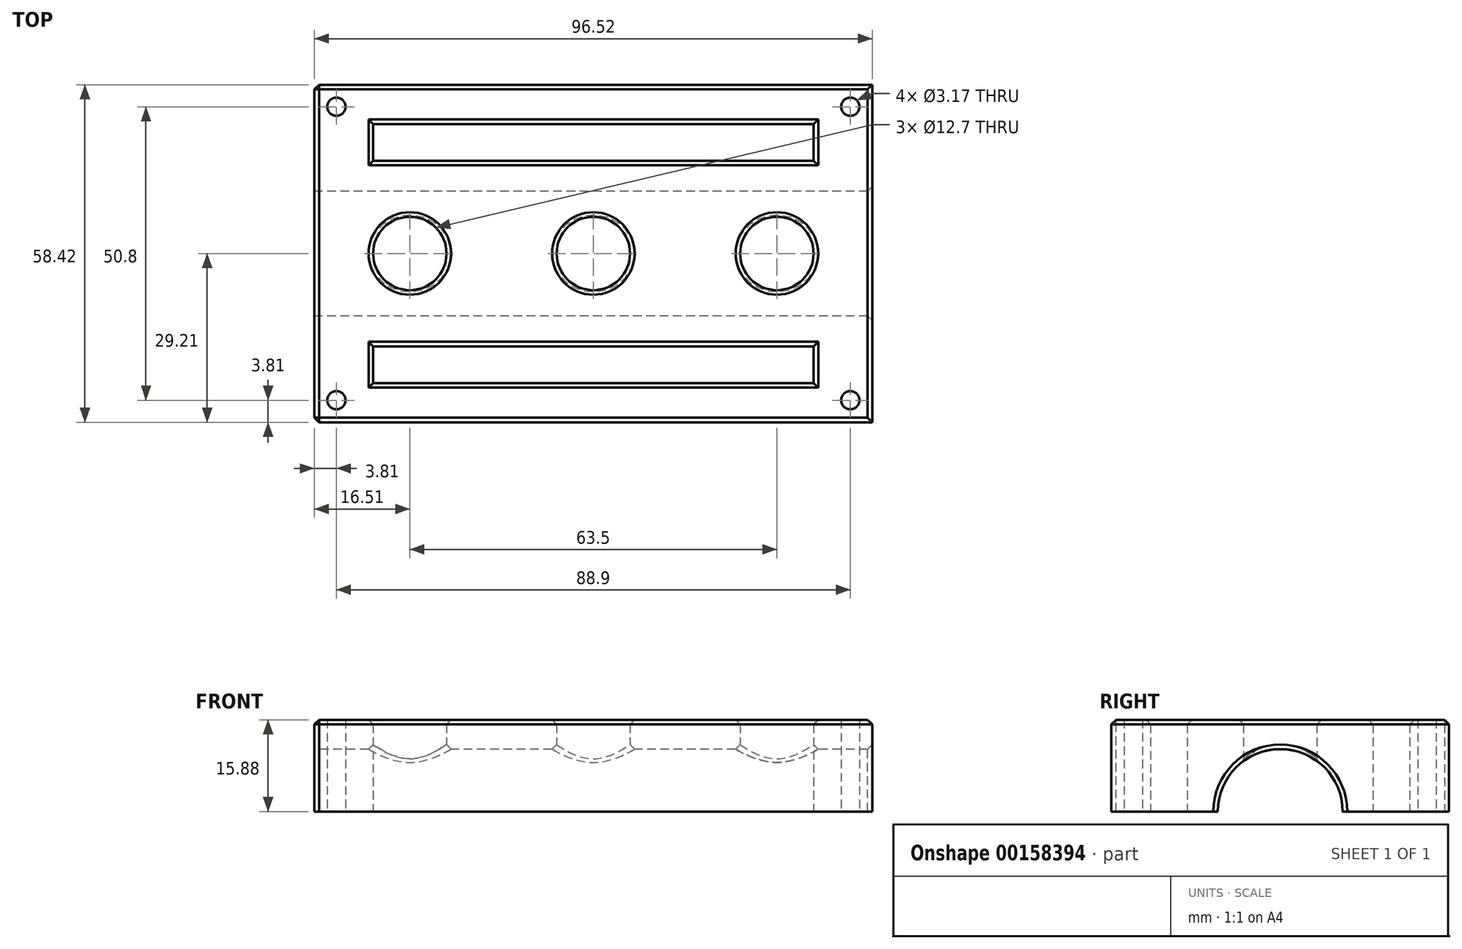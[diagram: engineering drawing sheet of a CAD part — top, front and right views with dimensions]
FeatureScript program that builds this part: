
annotation { "Feature Type Name" : "Feature", "Feature Type Description" : "" }
export const myFeature = defineFeature(function(context is Context, id is Id, definition is map)
    precondition{}
    {
        {
            var Q0;
            Q0=qCreatedBy(makeId("Top.planeOp"),FACE);
            var sketch = newSketch(context, id + "F0", { "sketchPlane" : qUnion([Q0])});
            skLineSegment(sketch, "E0", {"start": v(0, 0) * mm, "end": v(-48.26, 0) * mm});
            skLineSegment(sketch, "E1", {"start": v(-48.26, 0) * mm, "end": v(-48.26, 29.21) * mm});
            skLineSegment(sketch, "E2", {"start": v(-48.26, 29.21) * mm, "end": v(0, 29.21) * mm});
            skLineSegment(sketch, "E3", {"start": v(0, 29.21) * mm, "end": v(0, 0) * mm});
            skLineSegment(sketch, "E4.MirrorCS", {"start": v(48.26, 29.21) * mm, "end": v(0, 29.21) * mm});
            skLineSegment(sketch, "E5.MirrorCS", {"start": v(48.26, 0) * mm, "end": v(48.26, 29.21) * mm});
            skLineSegment(sketch, "E6.MirrorCS", {"start": v(0, 0) * mm, "end": v(48.26, 0) * mm});
            skLineSegment(sketch, "E7.MirrorCS", {"start": v(-48.26, -29.21) * mm, "end": v(0, -29.21) * mm});
            skLineSegment(sketch, "E8.MirrorCS", {"start": v(48.26, -29.2) * mm, "end": v(0, -29.21) * mm});
            skLineSegment(sketch, "E9.MirrorCS", {"start": v(48.26, 0) * mm, "end": v(48.26, -29.21) * mm});
            skLineSegment(sketch, "E10.MirrorCS", {"start": v(-48.26, 0) * mm, "end": v(-48.26, -29.21) * mm});
            skSolve(sketch);
        }
        {
            var Q0;
            Q0=qSketchRegion(id+"F0",true);
            var Q1;
            Q1=qSketchRegion(id+"F1MxHlLQY0lKD1c_1",true);
            extrude(context, id + "F1", {"entities" : qUnion([Q0, Q1]), "depth" : 15.88 * mm});
        }
        {
            var Q0;
            Q0=makeQuery(id+"F1.opExtrude","SWEPT_FACE",FACE,{"disambiguationData":[OSD([sQuery(id+"F0.wireOp",EDGE,"E1"),sQuery(id+"F0.wireOp",EDGE,"E10.MirrorCS")])]});
            var sketch = newSketch(context, id + "F2", { "sketchPlane" : qUnion([Q0])});
            skCircle(sketch, "E11", {"center": v(0, 0) * mm, "radius": 10.8 * mm});
            skSolve(sketch);
        }
        {
            var Q0;
            Q0=qSketchRegion(id+"F2",true);
            extrude(context, id + "F3", {"entities" : qUnion([Q0]), "operationType" : NewBodyOperationType.REMOVE, "oppositeDirection" : true, "depth" : 101.6 * mm});
        }
        {
            var Q0;
            Q0=qCreatedBy(makeId("Top.planeOp"),FACE);
            var sketch = newSketch(context, id + "F4", { "sketchPlane" : qUnion([Q0])});
            skCircle(sketch, "E12", {"center": v(-44.45, 25.4) * mm, "radius": 1.59 * mm});
            skCircle(sketch, "E13.MirrorC", {"center": v(44.45, 25.4) * mm, "radius": 1.59 * mm});
            skCircle(sketch, "E14.MirrorC", {"center": v(44.45, -25.4) * mm, "radius": 1.59 * mm});
            skCircle(sketch, "E15.MirrorC", {"center": v(-44.45, -25.4) * mm, "radius": 1.59 * mm});
            skLineSegment(sketch, "E16.bottom", {"start": v(-38.1, 22.42) * mm, "end": v(38.1, 22.42) * mm});
            skLineSegment(sketch, "E16.top", {"start": v(-38.1, 16.07) * mm, "end": v(38.1, 16.07) * mm});
            skLineSegment(sketch, "E16.left", {"start": v(-38.1, 22.42) * mm, "end": v(-38.1, 16.07) * mm});
            skLineSegment(sketch, "E16.right", {"start": v(38.1, 22.42) * mm, "end": v(38.1, 16.07) * mm});
            skLineSegment(sketch, "E17.MirrorCS", {"start": v(-38.1, -16.07) * mm, "end": v(38.1, -16.07) * mm});
            skLineSegment(sketch, "E18.MirrorCS", {"start": v(-38.1, -22.42) * mm, "end": v(-38.1, -16.07) * mm});
            skLineSegment(sketch, "E19.MirrorCS", {"start": v(-38.1, -22.42) * mm, "end": v(38.1, -22.42) * mm});
            skLineSegment(sketch, "E20.MirrorCS", {"start": v(38.1, -22.42) * mm, "end": v(38.1, -16.07) * mm});
            skCircle(sketch, "E21", {"center": v(-31.75, 0) * mm, "radius": 6.35 * mm});
            skCircle(sketch, "E22", {"center": v(0, 0) * mm, "radius": 6.35 * mm});
            skCircle(sketch, "E23.MirrorC", {"center": v(31.75, 0) * mm, "radius": 6.35 * mm});
            skSolve(sketch);
        }
        {
            var Q0;
            Q0=qSketchRegion(id+"F4",true);
            extrude(context, id + "F5", {"entities" : qUnion([Q0]), "operationType" : NewBodyOperationType.REMOVE, "depth" : 25.4 * mm});
        }
        {
            var Q0;
            Q0=makeQuery(id+"F1.opExtrude","CAP_EDGE",EDGE,{"disambiguationData":[OSD([sQuery(id+"F0.wireOp",EDGE,"E2"),sQuery(id+"F0.wireOp",EDGE,"E4.MirrorCS")])],"isStart":false});
            var Q1;
            Q1=makeQuery(id+"F5.boolean.opBoolean","INTERSECT",EDGE,{"derivedFrom":[makeQuery(id+"F1.opExtrude","CAP_FACE",FACE,{"disambiguationData":[OSD([sQuery(id+"F0.wireOp",EDGE,"E1"),sQuery(id+"F0.wireOp",EDGE,"E2"),sQuery(id+"F0.wireOp",EDGE,"E4.MirrorCS"),sQuery(id+"F0.wireOp",EDGE,"E5.MirrorCS"),sQuery(id+"F0.wireOp",EDGE,"E7.MirrorCS"),sQuery(id+"F0.wireOp",EDGE,"E8.MirrorCS"),sQuery(id+"F0.wireOp",EDGE,"E9.MirrorCS"),sQuery(id+"F0.wireOp",EDGE,"E10.MirrorCS")])],"isStart":false}),makeQuery(id+"F5.opExtrude","SWEPT_FACE",FACE,{"disambiguationData":[OSD([sQuery(id+"F4.wireOp",EDGE,"E16.bottom")])]})]});
            var Q2;
            Q2=makeQuery(id+"F5.boolean.opBoolean","INTERSECT",EDGE,{"derivedFrom":[makeQuery(id+"F1.opExtrude","CAP_FACE",FACE,{"disambiguationData":[OSD([sQuery(id+"F0.wireOp",EDGE,"E1"),sQuery(id+"F0.wireOp",EDGE,"E2"),sQuery(id+"F0.wireOp",EDGE,"E4.MirrorCS"),sQuery(id+"F0.wireOp",EDGE,"E5.MirrorCS"),sQuery(id+"F0.wireOp",EDGE,"E7.MirrorCS"),sQuery(id+"F0.wireOp",EDGE,"E8.MirrorCS"),sQuery(id+"F0.wireOp",EDGE,"E9.MirrorCS"),sQuery(id+"F0.wireOp",EDGE,"E10.MirrorCS")])],"isStart":false}),makeQuery(id+"F5.opExtrude","SWEPT_FACE",FACE,{"disambiguationData":[OSD([sQuery(id+"F4.wireOp",EDGE,"E16.top")])]})]});
            var Q3;
            Q3=makeQuery(id+"F5.boolean.opBoolean","INTERSECT",EDGE,{"derivedFrom":[makeQuery(id+"F1.opExtrude","CAP_FACE",FACE,{"disambiguationData":[OSD([sQuery(id+"F0.wireOp",EDGE,"E1"),sQuery(id+"F0.wireOp",EDGE,"E2"),sQuery(id+"F0.wireOp",EDGE,"E4.MirrorCS"),sQuery(id+"F0.wireOp",EDGE,"E5.MirrorCS"),sQuery(id+"F0.wireOp",EDGE,"E7.MirrorCS"),sQuery(id+"F0.wireOp",EDGE,"E8.MirrorCS"),sQuery(id+"F0.wireOp",EDGE,"E9.MirrorCS"),sQuery(id+"F0.wireOp",EDGE,"E10.MirrorCS")])],"isStart":false}),makeQuery(id+"F5.opExtrude","SWEPT_FACE",FACE,{"disambiguationData":[OSD([sQuery(id+"F4.wireOp",EDGE,"E16.left")])]})]});
            var Q4;
            Q4=makeQuery(id+"F5.boolean.opBoolean","INTERSECT",EDGE,{"derivedFrom":[makeQuery(id+"F1.opExtrude","CAP_FACE",FACE,{"disambiguationData":[OSD([sQuery(id+"F0.wireOp",EDGE,"E1"),sQuery(id+"F0.wireOp",EDGE,"E2"),sQuery(id+"F0.wireOp",EDGE,"E4.MirrorCS"),sQuery(id+"F0.wireOp",EDGE,"E5.MirrorCS"),sQuery(id+"F0.wireOp",EDGE,"E7.MirrorCS"),sQuery(id+"F0.wireOp",EDGE,"E8.MirrorCS"),sQuery(id+"F0.wireOp",EDGE,"E9.MirrorCS"),sQuery(id+"F0.wireOp",EDGE,"E10.MirrorCS")])],"isStart":false}),makeQuery(id+"F5.opExtrude","SWEPT_FACE",FACE,{"disambiguationData":[OSD([sQuery(id+"F4.wireOp",EDGE,"E16.right")])]})]});
            var Q5;
            Q5=makeQuery(id+"F5.boolean.opBoolean","INTERSECT",EDGE,{"derivedFrom":[makeQuery(id+"F1.opExtrude","CAP_FACE",FACE,{"disambiguationData":[OSD([sQuery(id+"F0.wireOp",EDGE,"E1"),sQuery(id+"F0.wireOp",EDGE,"E2"),sQuery(id+"F0.wireOp",EDGE,"E4.MirrorCS"),sQuery(id+"F0.wireOp",EDGE,"E5.MirrorCS"),sQuery(id+"F0.wireOp",EDGE,"E7.MirrorCS"),sQuery(id+"F0.wireOp",EDGE,"E8.MirrorCS"),sQuery(id+"F0.wireOp",EDGE,"E9.MirrorCS"),sQuery(id+"F0.wireOp",EDGE,"E10.MirrorCS")])],"isStart":false}),makeQuery(id+"F5.opExtrude","SWEPT_FACE",FACE,{"disambiguationData":[OSD([sQuery(id+"F4.wireOp",EDGE,"E23.MirrorC")])]})]});
            var Q6;
            Q6=makeQuery(id+"F5.boolean.opBoolean","INTERSECT",EDGE,{"derivedFrom":[makeQuery(id+"F1.opExtrude","CAP_FACE",FACE,{"disambiguationData":[OSD([sQuery(id+"F0.wireOp",EDGE,"E1"),sQuery(id+"F0.wireOp",EDGE,"E2"),sQuery(id+"F0.wireOp",EDGE,"E4.MirrorCS"),sQuery(id+"F0.wireOp",EDGE,"E5.MirrorCS"),sQuery(id+"F0.wireOp",EDGE,"E7.MirrorCS"),sQuery(id+"F0.wireOp",EDGE,"E8.MirrorCS"),sQuery(id+"F0.wireOp",EDGE,"E9.MirrorCS"),sQuery(id+"F0.wireOp",EDGE,"E10.MirrorCS")])],"isStart":false}),makeQuery(id+"F5.opExtrude","SWEPT_FACE",FACE,{"disambiguationData":[OSD([sQuery(id+"F4.wireOp",EDGE,"E22")])]})]});
            var Q7;
            Q7=makeQuery(id+"F5.boolean.opBoolean","INTERSECT",EDGE,{"derivedFrom":[makeQuery(id+"F1.opExtrude","CAP_FACE",FACE,{"disambiguationData":[OSD([sQuery(id+"F0.wireOp",EDGE,"E1"),sQuery(id+"F0.wireOp",EDGE,"E2"),sQuery(id+"F0.wireOp",EDGE,"E4.MirrorCS"),sQuery(id+"F0.wireOp",EDGE,"E5.MirrorCS"),sQuery(id+"F0.wireOp",EDGE,"E7.MirrorCS"),sQuery(id+"F0.wireOp",EDGE,"E8.MirrorCS"),sQuery(id+"F0.wireOp",EDGE,"E9.MirrorCS"),sQuery(id+"F0.wireOp",EDGE,"E10.MirrorCS")])],"isStart":false}),makeQuery(id+"F5.opExtrude","SWEPT_FACE",FACE,{"disambiguationData":[OSD([sQuery(id+"F4.wireOp",EDGE,"E21")])]})]});
            var Q8;
            Q8=makeQuery(id+"F5.boolean.opBoolean","INTERSECT",EDGE,{"derivedFrom":[makeQuery(id+"F1.opExtrude","CAP_FACE",FACE,{"disambiguationData":[OSD([sQuery(id+"F0.wireOp",EDGE,"E1"),sQuery(id+"F0.wireOp",EDGE,"E2"),sQuery(id+"F0.wireOp",EDGE,"E4.MirrorCS"),sQuery(id+"F0.wireOp",EDGE,"E5.MirrorCS"),sQuery(id+"F0.wireOp",EDGE,"E7.MirrorCS"),sQuery(id+"F0.wireOp",EDGE,"E8.MirrorCS"),sQuery(id+"F0.wireOp",EDGE,"E9.MirrorCS"),sQuery(id+"F0.wireOp",EDGE,"E10.MirrorCS")])],"isStart":false}),makeQuery(id+"F5.opExtrude","SWEPT_FACE",FACE,{"disambiguationData":[OSD([sQuery(id+"F4.wireOp",EDGE,"E17.MirrorCS")])]})]});
            var Q9;
            Q9=makeQuery(id+"F5.boolean.opBoolean","INTERSECT",EDGE,{"derivedFrom":[makeQuery(id+"F1.opExtrude","CAP_FACE",FACE,{"disambiguationData":[OSD([sQuery(id+"F0.wireOp",EDGE,"E1"),sQuery(id+"F0.wireOp",EDGE,"E2"),sQuery(id+"F0.wireOp",EDGE,"E4.MirrorCS"),sQuery(id+"F0.wireOp",EDGE,"E5.MirrorCS"),sQuery(id+"F0.wireOp",EDGE,"E7.MirrorCS"),sQuery(id+"F0.wireOp",EDGE,"E8.MirrorCS"),sQuery(id+"F0.wireOp",EDGE,"E9.MirrorCS"),sQuery(id+"F0.wireOp",EDGE,"E10.MirrorCS")])],"isStart":false}),makeQuery(id+"F5.opExtrude","SWEPT_FACE",FACE,{"disambiguationData":[OSD([sQuery(id+"F4.wireOp",EDGE,"E19.MirrorCS")])]})]});
            var Q10;
            Q10=makeQuery(id+"F5.boolean.opBoolean","INTERSECT",EDGE,{"derivedFrom":[makeQuery(id+"F1.opExtrude","CAP_FACE",FACE,{"disambiguationData":[OSD([sQuery(id+"F0.wireOp",EDGE,"E1"),sQuery(id+"F0.wireOp",EDGE,"E2"),sQuery(id+"F0.wireOp",EDGE,"E4.MirrorCS"),sQuery(id+"F0.wireOp",EDGE,"E5.MirrorCS"),sQuery(id+"F0.wireOp",EDGE,"E7.MirrorCS"),sQuery(id+"F0.wireOp",EDGE,"E8.MirrorCS"),sQuery(id+"F0.wireOp",EDGE,"E9.MirrorCS"),sQuery(id+"F0.wireOp",EDGE,"E10.MirrorCS")])],"isStart":false}),makeQuery(id+"F5.opExtrude","SWEPT_FACE",FACE,{"disambiguationData":[OSD([sQuery(id+"F4.wireOp",EDGE,"E18.MirrorCS")])]})]});
            var Q11;
            Q11=makeQuery(id+"F5.boolean.opBoolean","INTERSECT",EDGE,{"derivedFrom":[makeQuery(id+"F1.opExtrude","CAP_FACE",FACE,{"disambiguationData":[OSD([sQuery(id+"F0.wireOp",EDGE,"E1"),sQuery(id+"F0.wireOp",EDGE,"E2"),sQuery(id+"F0.wireOp",EDGE,"E4.MirrorCS"),sQuery(id+"F0.wireOp",EDGE,"E5.MirrorCS"),sQuery(id+"F0.wireOp",EDGE,"E7.MirrorCS"),sQuery(id+"F0.wireOp",EDGE,"E8.MirrorCS"),sQuery(id+"F0.wireOp",EDGE,"E9.MirrorCS"),sQuery(id+"F0.wireOp",EDGE,"E10.MirrorCS")])],"isStart":false}),makeQuery(id+"F5.opExtrude","SWEPT_FACE",FACE,{"disambiguationData":[OSD([sQuery(id+"F4.wireOp",EDGE,"E20.MirrorCS")])]})]});
            var Q12;
            Q12=makeQuery(id+"F3.boolean.opBoolean","COPY",EDGE,{"derivedFrom":makeQuery(id+"F3.opExtrude","CAP_EDGE",EDGE,{"disambiguationData":[OSD([sQuery(id+"F2.wireOp",EDGE,"E11")])],"isStart":true})});
            var Q13;
            Q13=makeQuery(id+"F1.opExtrude","CAP_EDGE",EDGE,{"disambiguationData":[OSD([sQuery(id+"F0.wireOp",EDGE,"E1"),sQuery(id+"F0.wireOp",EDGE,"E10.MirrorCS")])],"isStart":false});
            var Q14;
            Q14=makeQuery(id+"F1.opExtrude","SWEPT_EDGE",EDGE,{"disambiguationData":[OSD([sQuery(id+"F0.wireOp",EDGE,"E7.MirrorCS"),sQuery(id+"F0.wireOp",EDGE,"E10.MirrorCS")])]});
            var Q15;
            Q15=makeQuery(id+"F1.opExtrude","SWEPT_EDGE",EDGE,{"disambiguationData":[OSD([sQuery(id+"F0.wireOp",EDGE,"E1"),sQuery(id+"F0.wireOp",EDGE,"E2")])]});
            var Q16;
            Q16=makeQuery(id+"F3.boolean.opBoolean","INTERSECT",EDGE,{"derivedFrom":[makeQuery(id+"F1.opExtrude","SWEPT_FACE",FACE,{"disambiguationData":[OSD([sQuery(id+"F0.wireOp",EDGE,"E5.MirrorCS"),sQuery(id+"F0.wireOp",EDGE,"E9.MirrorCS")])]}),makeQuery(id+"F3.opExtrude","SWEPT_FACE",FACE,{"disambiguationData":[OSD([sQuery(id+"F2.wireOp",EDGE,"E11")])]})]});
            var Q17;
            Q17=makeQuery(id+"F1.opExtrude","CAP_EDGE",EDGE,{"disambiguationData":[OSD([sQuery(id+"F0.wireOp",EDGE,"E5.MirrorCS"),sQuery(id+"F0.wireOp",EDGE,"E9.MirrorCS")])],"isStart":false});
            var Q18;
            Q18=makeQuery(id+"F1.opExtrude","CAP_EDGE",EDGE,{"disambiguationData":[OSD([sQuery(id+"F0.wireOp",EDGE,"E7.MirrorCS"),sQuery(id+"F0.wireOp",EDGE,"E8.MirrorCS")])],"isStart":false});
            var Q19;
            Q19=makeQuery(id+"F5.boolean.opBoolean","COPY",EDGE,{"derivedFrom":makeQuery(id+"F5.opExtrude","CAP_EDGE",EDGE,{"disambiguationData":[OSD([sQuery(id+"F4.wireOp",EDGE,"E16.bottom")])],"isStart":true})});
            var Q20;
            Q20=makeQuery(id+"F5.boolean.opBoolean","COPY",EDGE,{"derivedFrom":makeQuery(id+"F5.opExtrude","CAP_EDGE",EDGE,{"disambiguationData":[OSD([sQuery(id+"F4.wireOp",EDGE,"E16.right")])],"isStart":true})});
            var Q21;
            Q21=makeQuery(id+"F5.boolean.opBoolean","COPY",EDGE,{"derivedFrom":makeQuery(id+"F5.opExtrude","CAP_EDGE",EDGE,{"disambiguationData":[OSD([sQuery(id+"F4.wireOp",EDGE,"E16.top")])],"isStart":true})});
            var Q22;
            Q22=makeQuery(id+"F5.boolean.opBoolean","COPY",EDGE,{"derivedFrom":makeQuery(id+"F5.opExtrude","CAP_EDGE",EDGE,{"disambiguationData":[OSD([sQuery(id+"F4.wireOp",EDGE,"E16.left")])],"isStart":true})});
            var Q23;
            Q23=makeQuery(id+"F5.boolean.opBoolean","COPY",EDGE,{"derivedFrom":makeQuery(id+"F5.opExtrude","CAP_EDGE",EDGE,{"disambiguationData":[OSD([sQuery(id+"F4.wireOp",EDGE,"E17.MirrorCS")])],"isStart":true})});
            var Q24;
            Q24=makeQuery(id+"F5.boolean.opBoolean","COPY",EDGE,{"derivedFrom":makeQuery(id+"F5.opExtrude","CAP_EDGE",EDGE,{"disambiguationData":[OSD([sQuery(id+"F4.wireOp",EDGE,"E19.MirrorCS")])],"isStart":true})});
            var Q25;
            Q25=makeQuery(id+"F5.boolean.opBoolean","COPY",EDGE,{"derivedFrom":makeQuery(id+"F5.opExtrude","CAP_EDGE",EDGE,{"disambiguationData":[OSD([sQuery(id+"F4.wireOp",EDGE,"E20.MirrorCS")])],"isStart":true})});
            var Q26;
            Q26=makeQuery(id+"F5.boolean.opBoolean","COPY",EDGE,{"derivedFrom":makeQuery(id+"F5.opExtrude","CAP_EDGE",EDGE,{"disambiguationData":[OSD([sQuery(id+"F4.wireOp",EDGE,"E18.MirrorCS")])],"isStart":true})});
            var Q27;
            Q27=makeQuery(id+"F5.boolean.opBoolean","INTERSECT",EDGE,{"derivedFrom":[makeQuery(id+"F3.boolean.opBoolean","COPY",FACE,{"derivedFrom":makeQuery(id+"F3.opExtrude","SWEPT_FACE",FACE,{"disambiguationData":[OSD([sQuery(id+"F2.wireOp",EDGE,"E11")])]})}),makeQuery(id+"F5.opExtrude","SWEPT_FACE",FACE,{"disambiguationData":[OSD([sQuery(id+"F4.wireOp",EDGE,"E23.MirrorC")])]})]});
            var Q28;
            Q28=makeQuery(id+"F5.boolean.opBoolean","INTERSECT",EDGE,{"derivedFrom":[makeQuery(id+"F3.boolean.opBoolean","COPY",FACE,{"derivedFrom":makeQuery(id+"F3.opExtrude","SWEPT_FACE",FACE,{"disambiguationData":[OSD([sQuery(id+"F2.wireOp",EDGE,"E11")])]})}),makeQuery(id+"F5.opExtrude","SWEPT_FACE",FACE,{"disambiguationData":[OSD([sQuery(id+"F4.wireOp",EDGE,"E22")])]})]});
            var Q29;
            Q29=makeQuery(id+"F5.boolean.opBoolean","INTERSECT",EDGE,{"derivedFrom":[makeQuery(id+"F3.boolean.opBoolean","COPY",FACE,{"derivedFrom":makeQuery(id+"F3.opExtrude","SWEPT_FACE",FACE,{"disambiguationData":[OSD([sQuery(id+"F2.wireOp",EDGE,"E11")])]})}),makeQuery(id+"F5.opExtrude","SWEPT_FACE",FACE,{"disambiguationData":[OSD([sQuery(id+"F4.wireOp",EDGE,"E21")])]})]});
            chamfer(context, id + "F6", {"entities" : qUnion([Q0, Q1, Q2, Q3, Q4, Q5, Q6, Q7, Q8, Q9, Q10, Q11, Q12, Q13, Q14, Q15, Q16, Q17, Q18, Q19, Q20, Q21, Q22, Q23, Q24, Q25, Q26, Q27, Q28, Q29]), "width" : 0.8 * mm, "tangentPropagation" : true});
        }
    });
